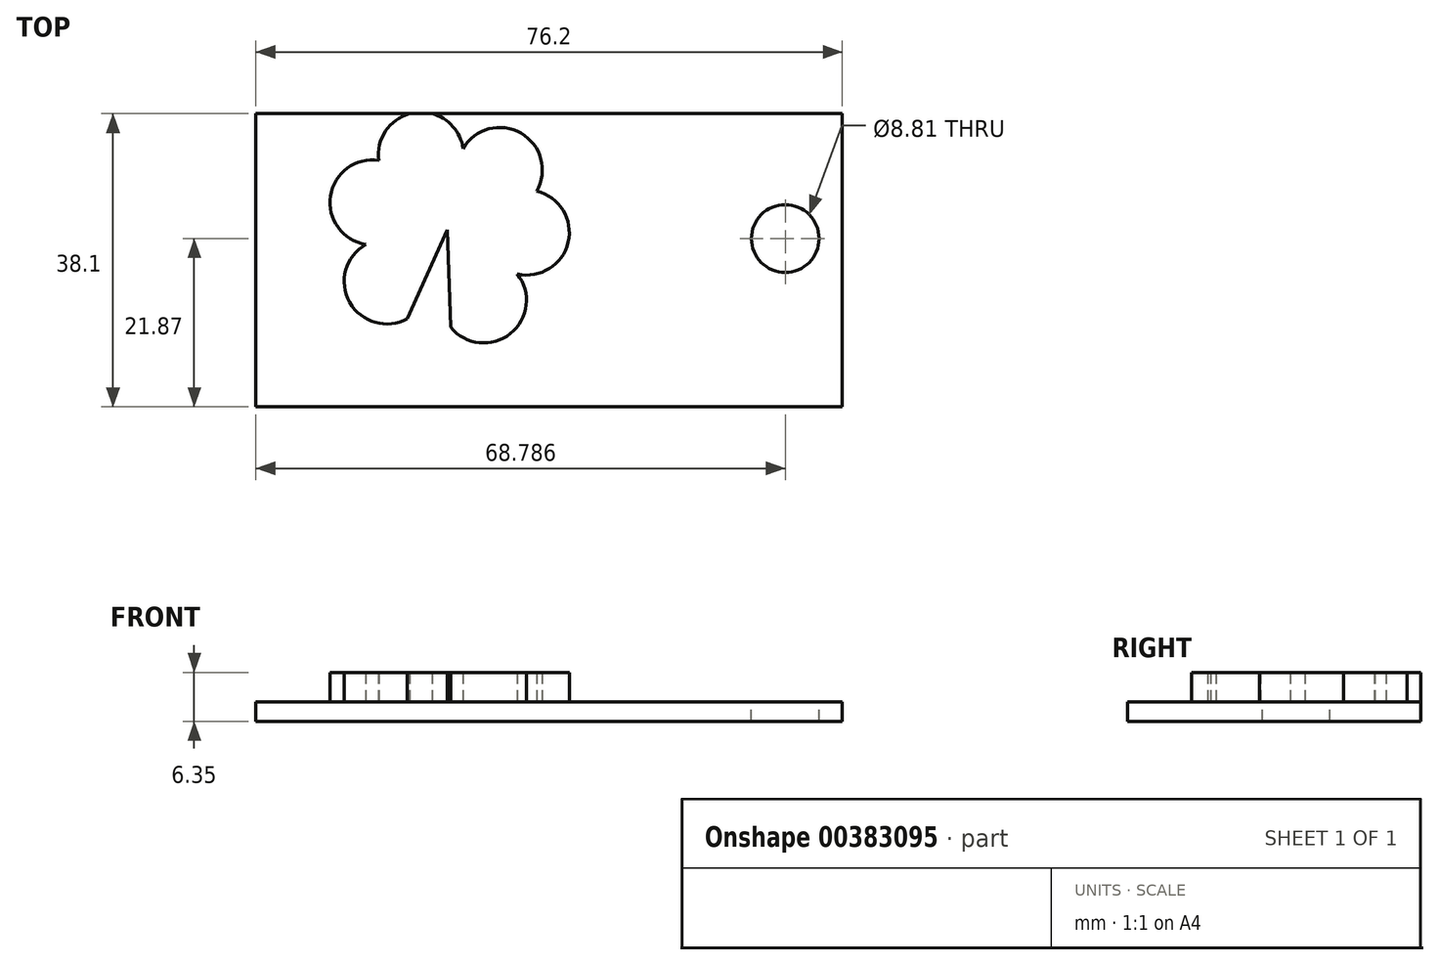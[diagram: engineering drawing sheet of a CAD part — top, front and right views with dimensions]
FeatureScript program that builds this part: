
annotation { "Feature Type Name" : "Feature", "Feature Type Description" : "" }
export const myFeature = defineFeature(function(context is Context, id is Id, definition is map)
    precondition{}
    {
        {
            var Q0;
            Q0=qCreatedBy(makeId("Top.planeOp"),FACE);
            var sketch = newSketch(context, id + "F0", { "sketchPlane" : qUnion([Q0])});
            skLineSegment(sketch, "E0.bottom", {"start": v(-60.44, 16.23) * mm, "end": v(15.76, 16.23) * mm});
            skLineSegment(sketch, "E0.top", {"start": v(-60.44, -21.87) * mm, "end": v(15.76, -21.87) * mm});
            skLineSegment(sketch, "E0.left", {"start": v(-60.44, 16.23) * mm, "end": v(-60.44, -21.87) * mm});
            skLineSegment(sketch, "E0.right", {"start": v(15.76, 16.23) * mm, "end": v(15.76, -21.87) * mm});
            skSolve(sketch);
        }
        {
            var Q0;
            Q0=makeQuery(id+"F0.imprint","IMPRINT",FACE,{"disambiguationData":[TD([[makeQuery(id+"F0.imprint","IMPRINT",EDGE,{"derivedFrom":sQuery(id+"F0.wireOp",EDGE,"E0.bottom")}),-1.0]])]});
            extrude(context, id + "F1", {"entities" : qUnion([Q0]), "depth" : 2.54 * mm});
        }
        {
            var Q0;
            Q0=makeQuery(id+"F1.opExtrude","CAP_FACE",FACE,{"disambiguationData":[OSD([sQuery(id+"F0.wireOp",EDGE,"E0.bottom"),sQuery(id+"F0.wireOp",EDGE,"E0.top"),sQuery(id+"F0.wireOp",EDGE,"E0.left"),sQuery(id+"F0.wireOp",EDGE,"E0.right")])],"isStart":false});
            var sketch = newSketch(context, id + "F2", { "sketchPlane" : qUnion([Q0])});
            skCircle(sketch, "E1", {"center": v(8.35, 0) * mm, "radius": 4.4 * mm});
            skSolve(sketch);
        }
        {
            var Q0;
            Q0=makeQuery(id+"F2.imprint","IMPRINT",FACE,{"disambiguationData":[TD([[makeQuery(id+"F2.imprint","IMPRINT",EDGE,{"derivedFrom":sQuery(id+"F2.wireOp",EDGE,"E1")}),1.0]])]});
            extrude(context, id + "F3", {"entities" : qUnion([Q0]), "operationType" : NewBodyOperationType.REMOVE, "oppositeDirection" : true, "depth" : 21.08 * mm});
        }
        {
            var Q0;
            Q0=makeQuery(id+"F1.opExtrude","CAP_FACE",FACE,{"disambiguationData":[OSD([sQuery(id+"F0.wireOp",EDGE,"E0.bottom"),sQuery(id+"F0.wireOp",EDGE,"E0.top"),sQuery(id+"F0.wireOp",EDGE,"E0.left"),sQuery(id+"F0.wireOp",EDGE,"E0.right")])],"isStart":false});
            var sketch = newSketch(context, id + "F4", { "sketchPlane" : qUnion([Q0])});
            skArc(sketch, "E2", {"start": v(-35.11, -11.51) * mm, "mid": v(-27.36, -12.35) * mm, "end": v(-26.48, -4.6) * mm});
            skLineSegment(sketch, "E3", {"start": v(-26.48, -4.6) * mm, "end": v(-35.57, 1.14) * mm});
            skLineSegment(sketch, "E4", {"start": v(-35.57, 1.14) * mm, "end": v(-35.11, -11.51) * mm});
            skArc(sketch, "E5.MirrorCS", {"start": v(-23.95, 6.16) * mm, "mid": v(-19.86, -0.48) * mm, "end": v(-26.48, -4.6) * mm});
            skLineSegment(sketch, "E6.MirrorCS", {"start": v(-35.57, 1.14) * mm, "end": v(-23.95, 6.16) * mm});
            skArc(sketch, "E7.MirrorCS", {"start": v(-23.95, 6.16) * mm, "mid": v(-25.98, 13.69) * mm, "end": v(-33.51, 11.7) * mm});
            skLineSegment(sketch, "E8.MirrorCS", {"start": v(-33.51, 11.7) * mm, "end": v(-35.57, 1.14) * mm});
            skArc(sketch, "E9.MirrorCS", {"start": v(-44.46, 10.16) * mm, "mid": v(-39.76, 16.37) * mm, "end": v(-33.51, 11.7) * mm});
            skLineSegment(sketch, "E10.MirrorCS", {"start": v(-35.57, 1.14) * mm, "end": v(-44.46, 10.16) * mm});
            skArc(sketch, "E11.MirrorCS", {"start": v(-44.46, 10.16) * mm, "mid": v(-50.74, 5.53) * mm, "end": v(-46.16, -0.77) * mm});
            skLineSegment(sketch, "E12.MirrorCS", {"start": v(-46.16, -0.77) * mm, "end": v(-35.57, 1.14) * mm});
            skArc(sketch, "E13.MirrorCS", {"start": v(-40.75, -10.41) * mm, "mid": v(-48.25, -8.28) * mm, "end": v(-46.16, -0.77) * mm});
            skLineSegment(sketch, "E14.MirrorCS", {"start": v(-35.57, 1.14) * mm, "end": v(-40.75, -10.41) * mm});
            skSolve(sketch);
        }
        {
            var Q0;
            Q0=makeQuery(id+"F4.imprint","IMPRINT",FACE,{"disambiguationData":[TD([[makeQuery(id+"F4.imprint","IMPRINT",EDGE,{"derivedFrom":sQuery(id+"F4.wireOp",EDGE,"E6.MirrorCS")}),1.0]])]});
            var Q1;
            Q1=makeQuery(id+"F4.imprint","IMPRINT",FACE,{"disambiguationData":[TD([[makeQuery(id+"F4.imprint","IMPRINT",EDGE,{"derivedFrom":sQuery(id+"F4.wireOp",EDGE,"E3")}),-1.0]])]});
            var Q2;
            Q2=makeQuery(id+"F4.imprint","IMPRINT",FACE,{"disambiguationData":[TD([[makeQuery(id+"F4.imprint","IMPRINT",EDGE,{"derivedFrom":sQuery(id+"F4.wireOp",EDGE,"E2")}),1.0]])]});
            var Q3;
            Q3=makeQuery(id+"F4.imprint","IMPRINT",FACE,{"disambiguationData":[TD([[makeQuery(id+"F4.imprint","IMPRINT",EDGE,{"derivedFrom":sQuery(id+"F4.wireOp",EDGE,"E12.MirrorCS")}),-1.0]])]});
            var Q4;
            Q4=makeQuery(id+"F4.imprint","IMPRINT",FACE,{"disambiguationData":[TD([[makeQuery(id+"F4.imprint","IMPRINT",EDGE,{"derivedFrom":sQuery(id+"F4.wireOp",EDGE,"E10.MirrorCS")}),1.0]])]});
            var Q5;
            {var subQ5=sQuery(id+"F4.wireOp",EDGE,"E8.MirrorCS");Q5=makeQuery(id+"F4.imprint","IMPRINT",FACE,{"disambiguationData":[TD([[makeQuery(id+"F4.imprint","IMPRINT",EDGE,{"derivedFrom":subQ5}),-1.0]])]});}
            extrude(context, id + "F5", {"entities" : qUnion([Q0, Q1, Q2, Q3, Q4, Q5]), "operationType" : NewBodyOperationType.ADD, "depth" : 3.8 * mm});
        }
    });
